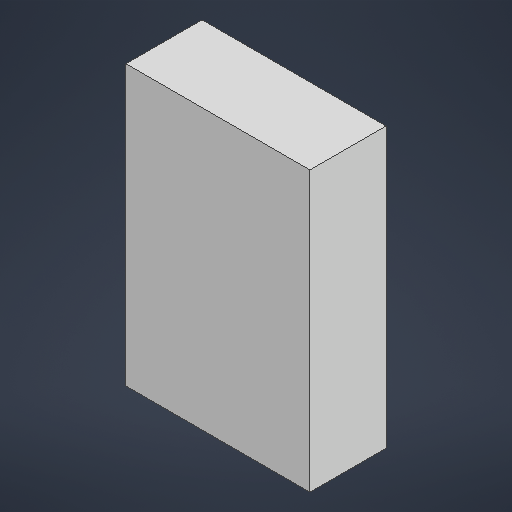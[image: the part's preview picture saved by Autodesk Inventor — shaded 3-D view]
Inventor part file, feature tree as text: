
AUTODESK INVENTOR PART (.ipt)
format: ipt  version: 2025.3 (Build 293356000, 356)  size: 158,208 bytes
history: native  units: mm
features: extrude x1, sketch x1
ambient origin geometry x8: Origin, YZ Plane, XZ Plane, XY Plane, X Axis, Y Axis, Z Axis, Center Point
bodies: Solid1 (feature_tree)
feature tree (2):
  extrude  "Extrusion1"  Depth=6.0mm
  sketch  "Sketch1"  dims[d0=14.5mm d1=6.0mm d2=22.0mm d3=0.0mm]
